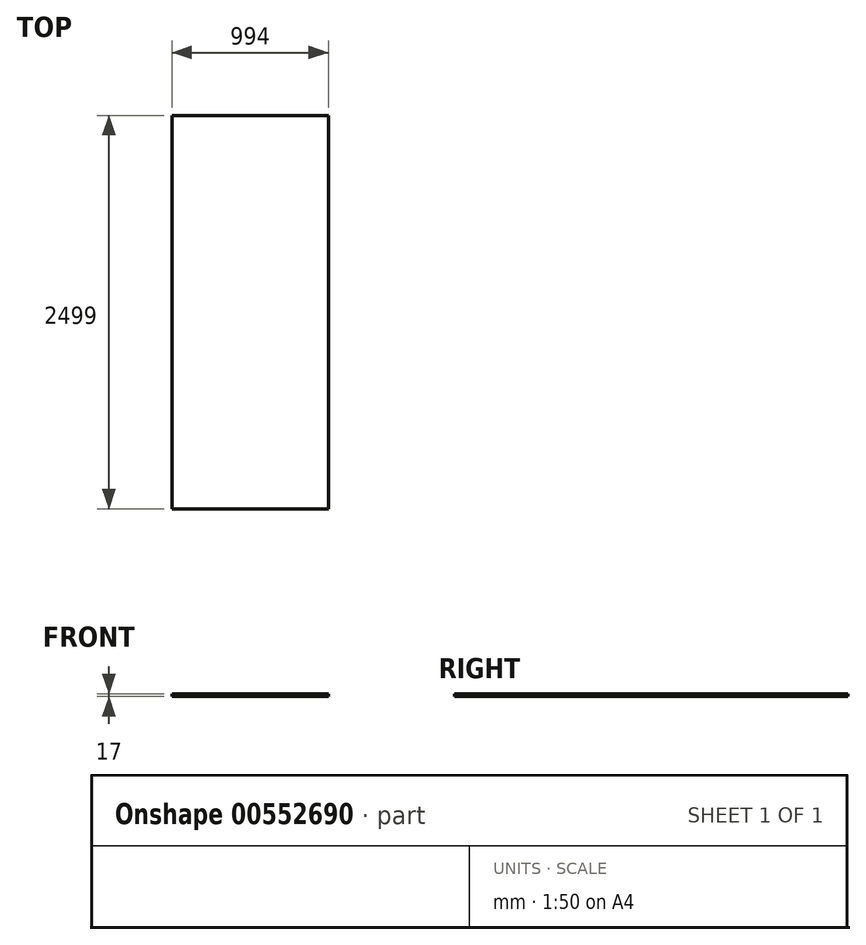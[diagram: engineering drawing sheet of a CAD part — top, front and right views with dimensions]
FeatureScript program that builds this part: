
annotation { "Feature Type Name" : "Feature", "Feature Type Description" : "" }
export const myFeature = defineFeature(function(context is Context, id is Id, definition is map)
    precondition{}
    {
        {
            var Q0;
            Q0=qCreatedBy(makeId("Top.planeOp"),FACE);
            var sketch = newSketch(context, id + "F0", { "sketchPlane" : qUnion([Q0])});
            skLineSegment(sketch, "E0.bottom", {"start": v(497, 1249.5) * mm, "end": v(-497, 1249.5) * mm});
            skLineSegment(sketch, "E0.top", {"start": v(497, -1249.5) * mm, "end": v(-497, -1249.5) * mm});
            skLineSegment(sketch, "E0.left", {"start": v(497, 1249.5) * mm, "end": v(497, -1249.5) * mm});
            skLineSegment(sketch, "E0.right", {"start": v(-497, 1249.5) * mm, "end": v(-497, -1249.5) * mm});
            skPoint(sketch, "E0.middle", {"position": v(0, 0) * mm});
            skSolve(sketch);
        }
        {
            var Q0;
            Q0 = qSketchRegion(id + "F0", true);
            extrude(context, id + "F1", {"entities" : qUnion([Q0]), "oppositeDirection" : true, "depth" : 17 * mm, "offsetDistance" : 25 * mm});
        }
    });
